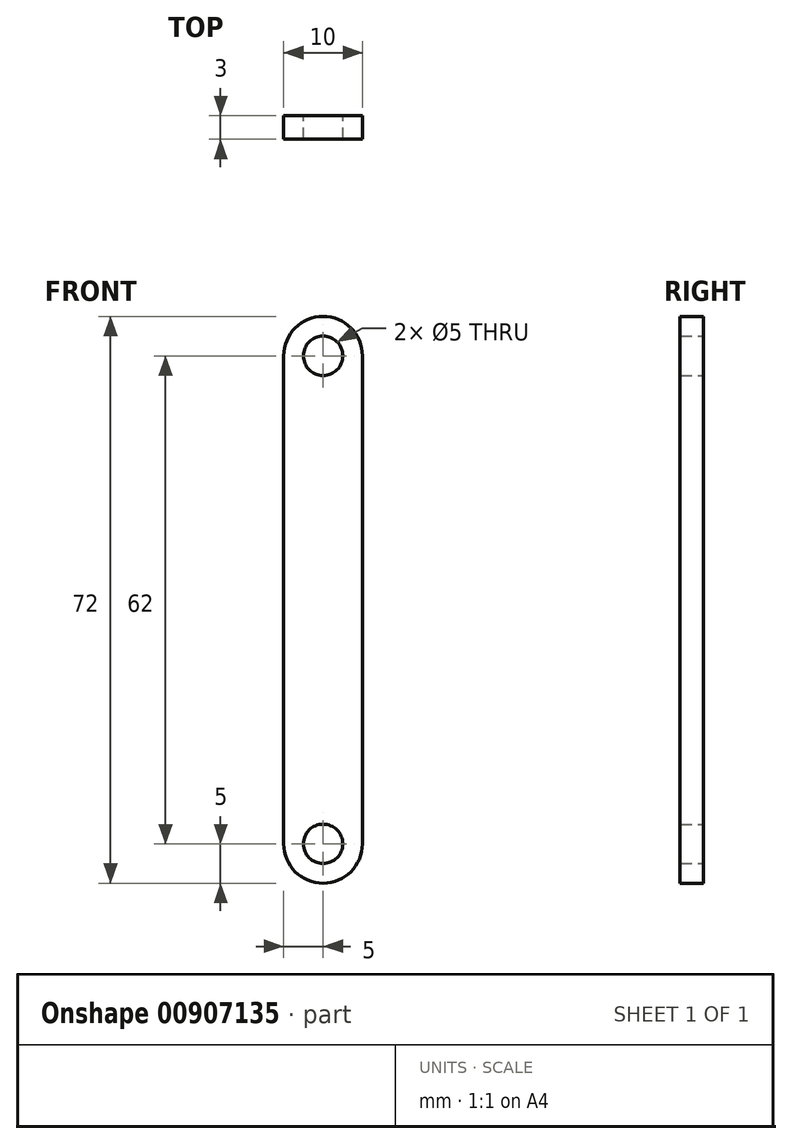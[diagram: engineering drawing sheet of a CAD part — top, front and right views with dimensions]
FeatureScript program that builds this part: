
annotation { "Feature Type Name" : "Feature", "Feature Type Description" : "" }
export const myFeature = defineFeature(function(context is Context, id is Id, definition is map)
    precondition{}
    {
        {
            var Q0;
            Q0=qCreatedBy(makeId("Front.planeOp"),FACE);
            var sketch = newSketch(context, id + "F0", { "sketchPlane" : qUnion([Q0])});
            skLineSegment(sketch, "E0.left", {"start": v(5, 31) * mm, "end": v(5, -31) * mm});
            skLineSegment(sketch, "E0.right", {"start": v(-5, 31) * mm, "end": v(-5, -31) * mm});
            skPoint(sketch, "E0.middle", {"position": v(0, 0) * mm});
            skArc(sketch, "E1", {"start": v(5, 31) * mm, "mid": v(0, 36) * mm, "end": v(-5, 31) * mm});
            skArc(sketch, "E2", {"start": v(-5, -31) * mm, "mid": v(0, -36) * mm, "end": v(5, -31) * mm});
            skCircle(sketch, "E3", {"center": v(0, 31) * mm, "radius": 2.5 * mm});
            skCircle(sketch, "E4", {"center": v(0, -31) * mm, "radius": 2.5 * mm});
            skSolve(sketch);
        }
        {
            var Q0;
            Q0=qSketchRegion(id+"F0",true);
            extrude(context, id + "F1", {"entities" : qUnion([Q0]), "depth" : 3 * mm, "offsetDistance" : 25 * mm});
        }
    });
